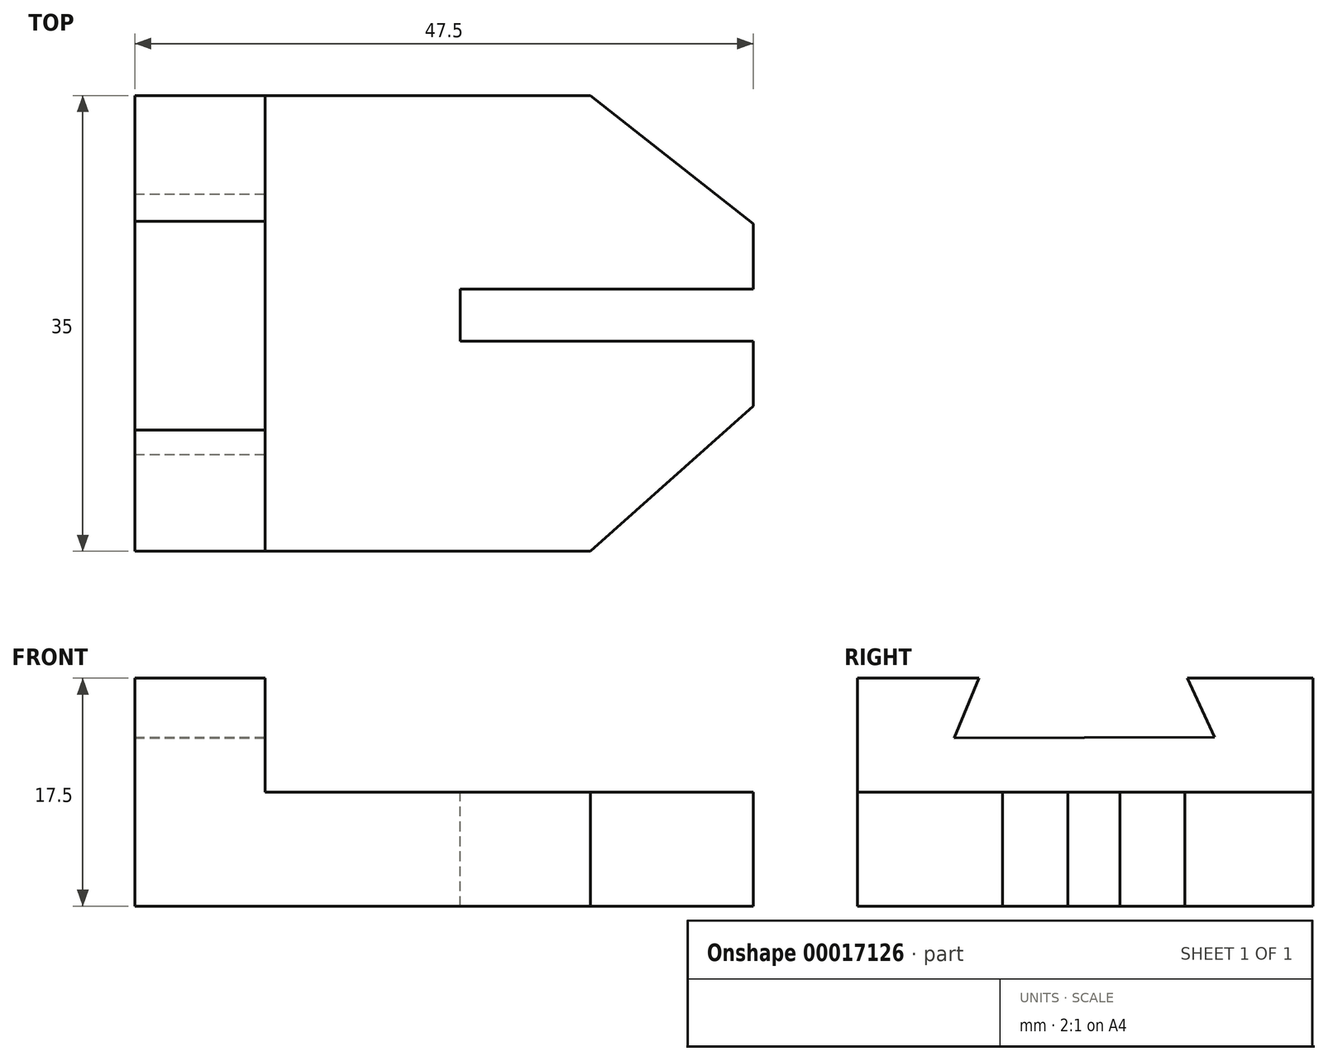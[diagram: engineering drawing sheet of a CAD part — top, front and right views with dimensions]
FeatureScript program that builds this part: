
annotation { "Feature Type Name" : "Feature", "Feature Type Description" : "" }
export const myFeature = defineFeature(function(context is Context, id is Id, definition is map)
    precondition{}
    {
        {
            var Q0;
            Q0=qCreatedBy(makeId("Right.planeOp"),FACE);
            var sketch = newSketch(context, id + "F0", { "sketchPlane" : qUnion([Q0])});
            skLineSegment(sketch, "E0.bottom", {"start": v(-21.12, 17.5) * mm, "end": v(13.88, 17.5) * mm});
            skLineSegment(sketch, "E0.top", {"start": v(-21.12, 0) * mm, "end": v(13.88, 0) * mm});
            skLineSegment(sketch, "E0.left", {"start": v(-21.12, 17.5) * mm, "end": v(-21.12, 0) * mm});
            skLineSegment(sketch, "E0.right", {"start": v(13.88, 17.5) * mm, "end": v(13.88, 0) * mm});
            skLineSegment(sketch, "E1.0", {"start": v(6.32, 12.96) * mm, "end": v(-13.68, 12.91) * mm});
            skLineSegment(sketch, "E1.1", {"start": v(-13.68, 12.91) * mm, "end": v(-11.8, 17.5) * mm});
            skLineSegment(sketch, "E1.4", {"start": v(4.22, 17.5) * mm, "end": v(6.32, 12.96) * mm});
            skPoint(sketch, "E1.0.midPoint", {"position": v(-3.68, 12.94) * mm});
            skPoint(sketch, "E2.orphan", {"position": v(-9.31, 23.54) * mm});
            skPoint(sketch, "E3.orphan", {"position": v(3.18, 19.75) * mm});
            skPoint(sketch, "E1.cCircle.center.orphan", {"position": v(-3.62, 17.5) * mm});
            skSolve(sketch);
        }
        {
            var Q0;
            Q0 = qSketchRegion(id + "F0", true);
            extrude(context, id + "F1", {"entities" : qUnion([Q0]), "oppositeDirection" : true, "depth" : 10 * mm});
        }
        {
            var Q0;
            Q0=makeQuery(id+"F0.imprint","IMPRINT",FACE,{"disambiguationData":[TD([[makeQuery(id+"F0.imprint","IMPRINT",EDGE,{"derivedFrom":sQuery(id+"F0.wireOp",EDGE,"E1.0")}),-1.0]])]});
            extrude(context, id + "F2", {"entities" : qUnion([Q0]), "operationType" : NewBodyOperationType.REMOVE, "oppositeDirection" : true, "depth" : 19.18 * mm});
        }
        {
            var Q0;
            Q0=makeQuery(id+"F1.opExtrude","CAP_FACE",FACE,{"disambiguationData":[OSD([sQuery(id+"F0.wireOp",EDGE,"E0.bottom"),sQuery(id+"F0.wireOp",EDGE,"E0.top"),sQuery(id+"F0.wireOp",EDGE,"E0.left"),sQuery(id+"F0.wireOp",EDGE,"E0.right")])],"isStart":true});
            var sketch = newSketch(context, id + "F3", { "sketchPlane" : qUnion([Q0])});
            skLineSegment(sketch, "E4.bottom", {"start": v(-21.12, 0) * mm, "end": v(13.88, 0) * mm});
            skLineSegment(sketch, "E4.top", {"start": v(-21.12, 8.75) * mm, "end": v(13.88, 8.75) * mm});
            skLineSegment(sketch, "E4.left", {"start": v(-21.12, 0) * mm, "end": v(-21.12, 8.75) * mm});
            skLineSegment(sketch, "E4.right", {"start": v(13.88, 0) * mm, "end": v(13.88, 8.75) * mm});
            skSolve(sketch);
        }
        {
            var Q0;
            Q0 = qSketchRegion(id + "F3", true);
            extrude(context, id + "F4", {"entities" : qUnion([Q0]), "operationType" : NewBodyOperationType.ADD, "depth" : 37.5 * mm});
        }
        {
            var Q0;
            Q0=makeQuery(id+"F4.opExtrude","SWEPT_FACE",FACE,{"disambiguationData":[OSD([sQuery(id+"F3.wireOp",EDGE,"E4.top")])]});
            var sketch = newSketch(context, id + "F5", { "sketchPlane" : qUnion([Q0])});
            skLineSegment(sketch, "E5.bottom", {"start": v(37.5, -0.97) * mm, "end": v(15, -0.97) * mm});
            skLineSegment(sketch, "E5.top", {"start": v(37.5, -4.97) * mm, "end": v(15, -4.97) * mm});
            skLineSegment(sketch, "E5.left", {"start": v(37.5, -0.97) * mm, "end": v(37.5, -4.97) * mm});
            skLineSegment(sketch, "E5.right", {"start": v(15, -0.97) * mm, "end": v(15, -4.97) * mm});
            skLineSegment(sketch, "E6", {"start": v(37.5, -0.97) * mm, "end": v(37.5, 4.03) * mm});
            skLineSegment(sketch, "E7", {"start": v(37.5, -4.97) * mm, "end": v(37.5, -9.97) * mm});
            skLineSegment(sketch, "E8", {"start": v(37.5, 4.03) * mm, "end": v(25, 13.88) * mm});
            skLineSegment(sketch, "E9", {"start": v(37.5, -9.97) * mm, "end": v(25, -21.12) * mm});
            skSolve(sketch);
        }
        {
            var Q0;
            Q0 = qSketchRegion(id + "F5", true);
            extrude(context, id + "F6", {"entities" : qUnion([Q0]), "operationType" : NewBodyOperationType.REMOVE, "oppositeDirection" : true, "depth" : 18.03 * mm});
        }
        {
            var Q0;
            {var subQ2=sQuery(id+"F5.wireOp",EDGE,"E8");Q0=makeQuery(id+"F5.imprint","IMPRINT",FACE,{"disambiguationData":[TD([[makeQuery(id+"F5.imprint","IMPRINT",EDGE,{"derivedFrom":subQ2}),-1.0]])]});}
            extrude(context, id + "F7", {"entities" : qUnion([Q0]), "operationType" : NewBodyOperationType.REMOVE, "oppositeDirection" : true, "depth" : 25 * mm});
        }
        {
            var Q0;
            {var subQ2=sQuery(id+"F5.wireOp",EDGE,"E9");Q0=makeQuery(id+"F5.imprint","IMPRINT",FACE,{"disambiguationData":[TD([[makeQuery(id+"F5.imprint","IMPRINT",EDGE,{"derivedFrom":subQ2}),1.0]])]});}
            extrude(context, id + "F8", {"entities" : qUnion([Q0]), "operationType" : NewBodyOperationType.REMOVE, "oppositeDirection" : true, "depth" : 25 * mm});
        }
    });
